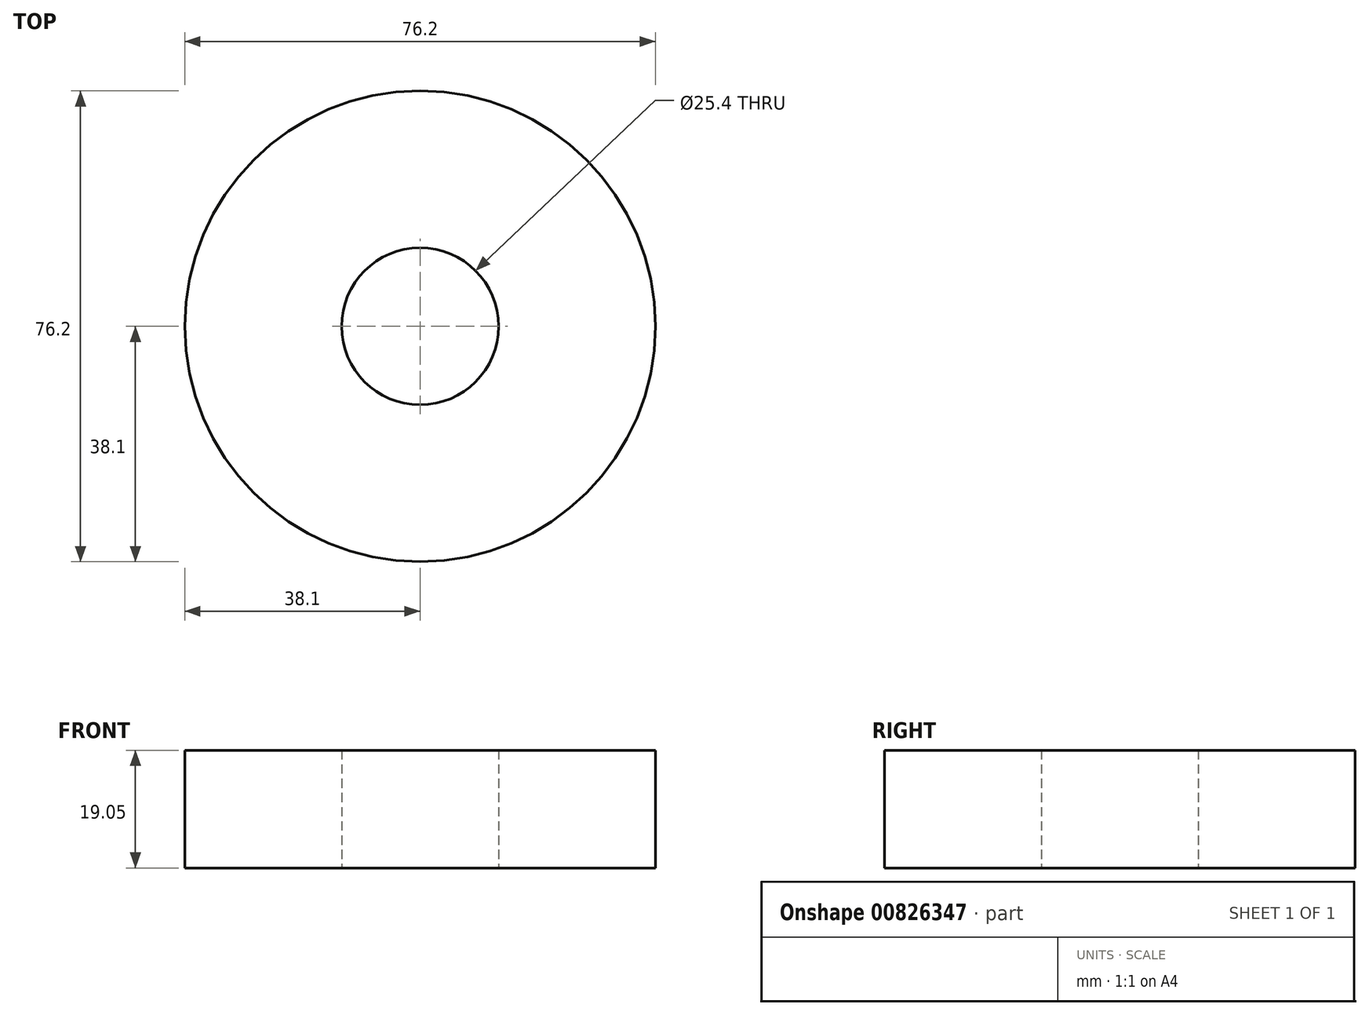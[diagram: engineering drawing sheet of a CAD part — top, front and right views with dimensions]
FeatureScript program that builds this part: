
annotation { "Feature Type Name" : "Feature", "Feature Type Description" : "" }
export const myFeature = defineFeature(function(context is Context, id is Id, definition is map)
    precondition{}
    {
        {
            var Q0;
            Q0=qCreatedBy(makeId("Top.planeOp"),FACE);
            var sketch = newSketch(context, id + "F0", { "sketchPlane" : qUnion([Q0])});
            skCircle(sketch, "E0", {"center": v(0, 0) * mm, "radius": 38.1 * mm});
            skCircle(sketch, "E1", {"center": v(0, 0) * mm, "radius": 12.7 * mm});
            skSolve(sketch);
        }
        {
            var Q0;
            Q0=makeQuery(id+"F0.imprint","IMPRINT",FACE,{"disambiguationData":[TD([[makeQuery(id+"F0.imprint","IMPRINT",EDGE,{"derivedFrom":sQuery(id+"F0.wireOp",EDGE,"E0")}),1.0]])]});
            extrude(context, id + "F1", {"entities" : qUnion([Q0]), "depth" : 19.05 * mm, "offsetDistance" : 25.4 * mm});
        }
    });
